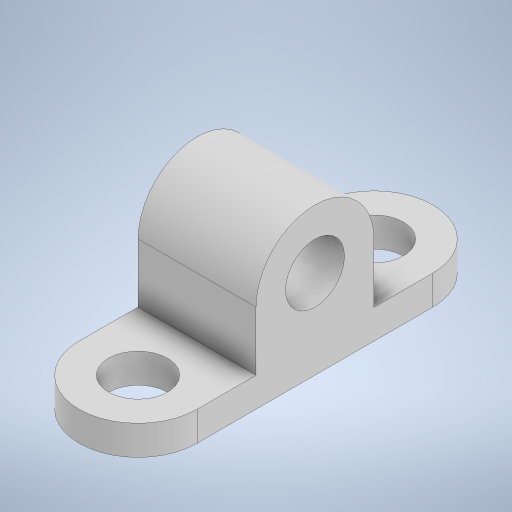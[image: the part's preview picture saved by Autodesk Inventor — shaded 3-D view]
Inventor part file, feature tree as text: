
AUTODESK INVENTOR PART (.ipt)
format: ipt  version: 2024 (Build 280153000, 153)  size: 253,952 bytes
history: native  units: mm
features: extrude x2, sketch x2, other x1
ambient origin geometry x8: Origin, YZ Plane, XZ Plane, XY Plane, X Axis, Y Axis, Z Axis, Center Point
bodies: Body1 (feature_tree)
feature tree (5):
  other  "Sólido1"
  extrude  "Extrusión1"  Depth=40.0mm
  extrude  "Extrusión2"  Depth=40.0mm
  sketch  "Boceto1"  dims[d4=20.0mm d5=40.0mm]
  sketch  "Boceto2"  dims[d6=20.0mm d7=40.0mm d8=10.0mm d9=0.0mm d11=40.0mm d12=20.0mm d13=40.0mm d14=0.0mm]
